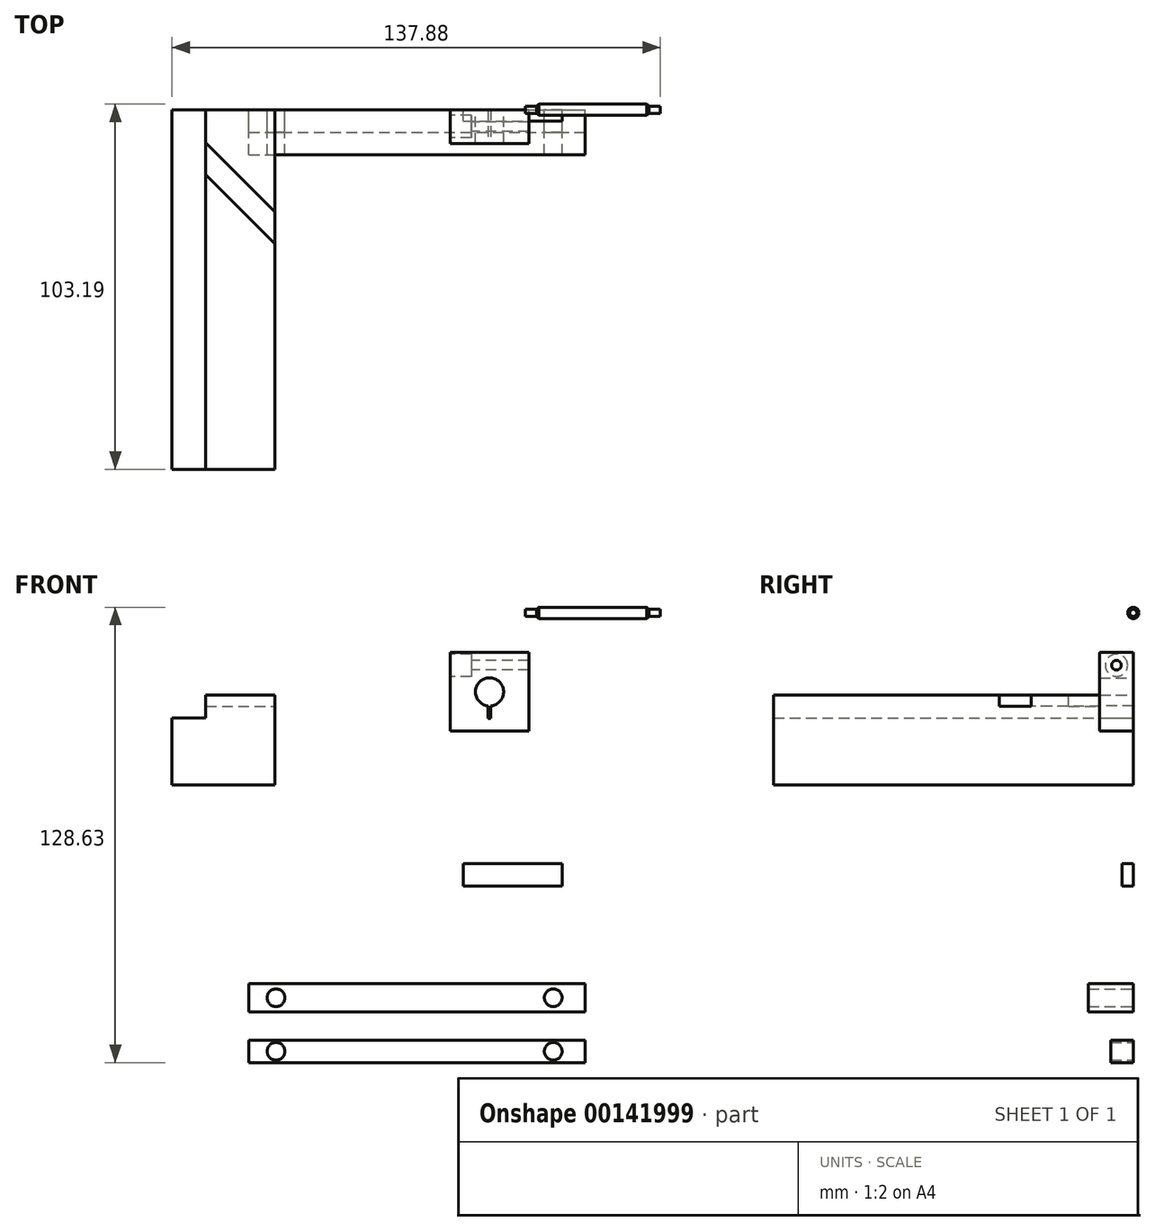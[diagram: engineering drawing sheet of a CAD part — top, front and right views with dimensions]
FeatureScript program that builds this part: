
annotation { "Feature Type Name" : "Feature", "Feature Type Description" : "" }
export const myFeature = defineFeature(function(context is Context, id is Id, definition is map)
    precondition{}
    {
        {
            var Q0;
            Q0=qCreatedBy(makeId("Front.planeOp"),FACE);
            var sketch = newSketch(context, id + "F0", { "sketchPlane" : qUnion([Q0])});
            skCircle(sketch, "E0", {"center": v(-55.23, 48.48) * mm, "radius": 3.97 * mm});
            skLineSegment(sketch, "E1.bottom", {"start": v(-44.12, 37.37) * mm, "end": v(-66.34, 37.37) * mm});
            skLineSegment(sketch, "E1.top", {"start": v(-44.12, 59.6) * mm, "end": v(-66.34, 59.6) * mm});
            skLineSegment(sketch, "E1.left", {"start": v(-44.12, 37.37) * mm, "end": v(-44.12, 59.6) * mm});
            skLineSegment(sketch, "E1.right", {"start": v(-66.34, 37.37) * mm, "end": v(-66.34, 59.6) * mm});
            skSolve(sketch);
        }
        {
            var Q0;
            Q0=makeQuery(id+"F0.imprint","IMPRINT",FACE,{"disambiguationData":[TD([[makeQuery(id+"F0.imprint","IMPRINT",EDGE,{"derivedFrom":sQuery(id+"F0.wireOp",EDGE,"E0")}),-1.0]])]});
            extrude(context, id + "F1", {"entities" : qUnion([Q0]), "depth" : 9.52 * mm});
        }
        {
            var Q0;
            Q0=makeQuery(id+"F1.opExtrude","SWEPT_FACE",FACE,{"disambiguationData":[OSD([sQuery(id+"F0.wireOp",EDGE,"E1.right")])]});
            var sketch = newSketch(context, id + "F2", { "sketchPlane" : qUnion([Q0])});
            skLineSegment(sketch, "E2.0", {"start": v(9.53, 59.6) * mm, "end": v(0, 59.6) * mm});
            skLineSegment(sketch, "E3.0", {"start": v(9.53, 37.37) * mm, "end": v(0, 37.37) * mm});
            skLineSegment(sketch, "E4", {"start": v(4.76, 59.6) * mm, "end": v(4.76, 52.45) * mm, "construction": true});
            skCircle(sketch, "E5", {"center": v(4.76, 48.48) * mm, "radius": 3.97 * mm});
            skLineSegment(sketch, "E6.trimOffspring", {"start": v(4.76, 44.51) * mm, "end": v(4.76, 37.37) * mm, "construction": true});
            skLineSegment(sketch, "E7", {"start": v(4.76, 48.48) * mm, "end": v(9.53, 48.48) * mm, "construction": true});
            skPoint(sketch, "E8", {"position": v(4.76, 56.02) * mm});
            skSolve(sketch);
        }
        {
            var Q0;
            Q0=sQuery(id+"F2.wireOp",VERTEX,"E8");
            var Q1;
            Q1=makeQuery(id+"F1.opExtrude","SWEPT_BODY",BODY,{"disambiguationData":[OSD([sQuery(id+"F0.wireOp",EDGE,"E0"),sQuery(id+"F0.wireOp",EDGE,"E1.bottom"),sQuery(id+"F0.wireOp",EDGE,"E1.top"),sQuery(id+"F0.wireOp",EDGE,"E1.left"),sQuery(id+"F0.wireOp",EDGE,"E1.right")])]});
            hole(context, id + "F3", {"style" : HoleStyle.C_BORE, "endStyle" : HoleEndStyle.THROUGH, "holeDiameter" : 2.7 * mm, "cBoreDiameter" : 6.35 * mm, "cBoreDepth" : 5.97 * mm, "tappedDepth" : 12.7 * mm, "tapClearance" : 3, "startFromSketch" : true, "locations" : qUnion([Q0]), "scope" : qUnion([Q1]), "majorDiameter" : 6.35 * mm});
        }
        {
            var Q0;
            Q0=makeQuery(id+"F1.opExtrude","CAP_FACE",FACE,{"disambiguationData":[OSD([sQuery(id+"F0.wireOp",EDGE,"E0"),sQuery(id+"F0.wireOp",EDGE,"E1.bottom"),sQuery(id+"F0.wireOp",EDGE,"E1.top"),sQuery(id+"F0.wireOp",EDGE,"E1.left"),sQuery(id+"F0.wireOp",EDGE,"E1.right")])],"isStart":false});
            var sketch = newSketch(context, id + "F4", { "sketchPlane" : qUnion([Q0])});
            skLineSegment(sketch, "E9.0", {"start": v(-44.12, 59.6) * mm, "end": v(-66.34, 59.6) * mm});
            skLineSegment(sketch, "E10.0", {"start": v(-44.12, 37.37) * mm, "end": v(-44.12, 59.6) * mm});
            skLineSegment(sketch, "E11.0", {"start": v(-66.34, 37.37) * mm, "end": v(-66.34, 59.6) * mm});
            skLineSegment(sketch, "E12.0", {"start": v(-44.12, 37.37) * mm, "end": v(-66.34, 37.37) * mm});
            skLineSegment(sketch, "E13", {"start": v(-55.63, 59.6) * mm, "end": v(-54.83, 59.6) * mm});
            skLineSegment(sketch, "E14", {"start": v(-55.23, 59.6) * mm, "end": v(-55.23, 48.48) * mm, "construction": true});
            skLineSegment(sketch, "E15.0", {"start": v(-55.63, 59.6) * mm, "end": v(-55.63, 40.94) * mm});
            skLineSegment(sketch, "E16.0", {"start": v(-54.83, 59.6) * mm, "end": v(-54.83, 40.94) * mm});
            skCircle(sketch, "E17.0", {"center": v(-55.23, 48.48) * mm, "radius": 3.97 * mm});
            skLineSegment(sketch, "E18.trimOffspring", {"start": v(-55.23, 44.51) * mm, "end": v(-55.23, 37.37) * mm, "construction": true});
            skLineSegment(sketch, "E19", {"start": v(-55.63, 40.94) * mm, "end": v(-54.83, 40.94) * mm});
            skPoint(sketch, "E19.startSnap0", {"position": v(-55.23, 40.94) * mm});
            skSolve(sketch);
        }
        {
            var Q0;
            {var subQ5=sQuery(id+"F4.wireOp",EDGE,"E13");Q0=makeQuery(id+"F4.imprint","IMPRINT",FACE,{"disambiguationData":[TD([[makeQuery(id+"F4.imprint","IMPRINT",EDGE,{"derivedFrom":subQ5}),1.0]])]});}
            var Q1;
            {var subQ0=sQuery(id+"F4.wireOp",EDGE,"E19");Q1=makeQuery(id+"F4.imprint","IMPRINT",FACE,{"disambiguationData":[TD([[makeQuery(id+"F4.imprint","IMPRINT",EDGE,{"derivedFrom":subQ0}),1.0]])]});}
            extrude(context, id + "F5", {"entities" : qUnion([Q0, Q1]), "operationType" : NewBodyOperationType.REMOVE, "oppositeDirection" : true, "depth" : 25.4 * mm});
        }
        {
            var Q0;
            Q0=qCreatedBy(makeId("Front.planeOp"),FACE);
            var sketch = newSketch(context, id + "F6", { "sketchPlane" : qUnion([Q0])});
            skLineSegment(sketch, "E20", {"start": v(-45.1, 70.79) * mm, "end": v(-7, 70.79) * mm});
            skLineSegment(sketch, "E21", {"start": v(-45.1, 70.79) * mm, "end": v(-45.1, 71.78) * mm});
            skLineSegment(sketch, "E22", {"start": v(-41.34, 72.38) * mm, "end": v(-10.78, 72.38) * mm});
            skLineSegment(sketch, "E23", {"start": v(-10.78, 72.38) * mm, "end": v(-10.18, 71.78) * mm});
            skLineSegment(sketch, "E24", {"start": v(-10.18, 71.78) * mm, "end": v(-7, 71.78) * mm});
            skLineSegment(sketch, "E25", {"start": v(-7, 71.78) * mm, "end": v(-7, 70.79) * mm});
            skLineSegment(sketch, "E26", {"start": v(-26.06, 70.79) * mm, "end": v(-26.06, 72.38) * mm, "construction": true});
            skLineSegment(sketch, "E27.MirrorCS", {"start": v(-41.34, 72.38) * mm, "end": v(-41.93, 71.78) * mm});
            skLineSegment(sketch, "E28.MirrorCS", {"start": v(-41.93, 71.78) * mm, "end": v(-45.1, 71.78) * mm});
            skLineSegment(sketch, "E29.MirrorCS", {"start": v(-45.1, 71.78) * mm, "end": v(-45.1, 70.79) * mm});
            skSolve(sketch);
        }
        {
            var Q0;
            Q0=makeQuery(id+"F6.imprint","IMPRINT",FACE,{"disambiguationData":[TD([[makeQuery(id+"F6.imprint","IMPRINT",EDGE,{"derivedFrom":sQuery(id+"F6.wireOp",EDGE,"E20")}),1.0]])]});
            var Q1;
            Q1=sQuery(id+"F6.wireOp",EDGE,"E22");
            var Q2;
            Q2=sQuery(id+"F6.wireOp",EDGE,"E27.MirrorCS");
            var Q3;
            Q3=sQuery(id+"F6.wireOp",EDGE,"E28.MirrorCS");
            var Q4;
            Q4=sQuery(id+"F6.wireOp",EDGE,"E29.MirrorCS");
            var Q5;
            Q5=sQuery(id+"F6.wireOp",EDGE,"E23");
            var Q6;
            Q6=sQuery(id+"F6.wireOp",EDGE,"E24");
            var Q7;
            Q7=sQuery(id+"F6.wireOp",EDGE,"E25");
            var Q8;
            Q8=sQuery(id+"F6.wireOp",EDGE,"E20");
            revolve(context, id + "F7", {"entities" : qUnion([Q0]), "surfaceEntities" : qUnion([Q1, Q2, Q3, Q4, Q5, Q6, Q7]), "axis" : qUnion([Q8]), "revolveType" : RevolveType.FULL});
        }
        {
            var Q0;
            Q0=qCreatedBy(makeId("Front.planeOp"),FACE);
            var sketch = newSketch(context, id + "F8", { "sketchPlane" : qUnion([Q0])});
            skLineSegment(sketch, "E30.bottom", {"start": v(-123.23, -33.97) * mm, "end": v(-28.24, -33.97) * mm});
            skLineSegment(sketch, "E30.top", {"start": v(-123.23, -41.9) * mm, "end": v(-28.24, -41.9) * mm});
            skLineSegment(sketch, "E30.left", {"start": v(-123.23, -33.97) * mm, "end": v(-123.23, -41.9) * mm});
            skLineSegment(sketch, "E30.right", {"start": v(-28.24, -33.97) * mm, "end": v(-28.24, -41.9) * mm});
            skLineSegment(sketch, "E31", {"start": v(-123.23, -37.93) * mm, "end": v(-28.24, -37.93) * mm, "construction": true});
            skCircle(sketch, "E32", {"center": v(-115.54, -37.93) * mm, "radius": 2.5 * mm});
            skCircle(sketch, "E33", {"center": v(-37.23, -37.93) * mm, "radius": 2.5 * mm});
            skSolve(sketch);
        }
        {
            var Q0;
            Q0 = qSketchRegion(id + "F8", true);
            extrude(context, id + "F9", {"entities" : qUnion([Q0]), "depth" : 12.7 * mm});
        }
        {
            var Q0;
            Q0=qCreatedBy(makeId("Front.planeOp"),FACE);
            var sketch = newSketch(context, id + "F10", { "sketchPlane" : qUnion([Q0])});
            skLineSegment(sketch, "E34.0", {"start": v(-123.23, -33.97) * mm, "end": v(-123.23, -41.9) * mm});
            skLineSegment(sketch, "E35.0", {"start": v(-123.23, -41.9) * mm, "end": v(-28.24, -41.9) * mm});
            skLineSegment(sketch, "E36.0", {"start": v(-28.24, -33.97) * mm, "end": v(-28.24, -41.9) * mm});
            skCircle(sketch, "E37.0", {"center": v(-37.23, -37.93) * mm, "radius": 2.5 * mm});
            skCircle(sketch, "E38.0", {"center": v(-115.54, -37.93) * mm, "radius": 2.5 * mm});
            skLineSegment(sketch, "E39.bottom", {"start": v(-123.23, -49.9) * mm, "end": v(-28.24, -49.9) * mm});
            skLineSegment(sketch, "E39.top", {"start": v(-123.23, -56.25) * mm, "end": v(-28.24, -56.25) * mm});
            skLineSegment(sketch, "E39.left", {"start": v(-123.23, -49.9) * mm, "end": v(-123.23, -56.25) * mm});
            skLineSegment(sketch, "E39.right", {"start": v(-28.24, -49.9) * mm, "end": v(-28.24, -56.25) * mm});
            skLineSegment(sketch, "E40", {"start": v(-123.23, -53.08) * mm, "end": v(-28.24, -53.08) * mm, "construction": true});
            skCircle(sketch, "E41", {"center": v(-115.54, -53.08) * mm, "radius": 2.5 * mm});
            skCircle(sketch, "E42", {"center": v(-37.23, -53.08) * mm, "radius": 2.5 * mm});
            skSolve(sketch);
        }
        {
            var Q0;
            Q0=makeQuery(id+"F10.imprint","IMPRINT",FACE,{"disambiguationData":[TD([[makeQuery(id+"F10.imprint","IMPRINT",EDGE,{"derivedFrom":sQuery(id+"F10.wireOp",EDGE,"E39.bottom")}),-1.0]])]});
            extrude(context, id + "F11", {"entities" : qUnion([Q0]), "depth" : 6.35 * mm});
        }
        {
            var Q0;
            Q0=qCreatedBy(makeId("Front.planeOp"),FACE);
            var sketch = newSketch(context, id + "F12", { "sketchPlane" : qUnion([Q0])});
            skLineSegment(sketch, "E43.bottom", {"start": v(-62.62, 0) * mm, "end": v(-34.69, 0) * mm});
            skLineSegment(sketch, "E43.top", {"start": v(-62.62, -6.35) * mm, "end": v(-34.69, -6.35) * mm});
            skLineSegment(sketch, "E43.left", {"start": v(-62.62, 0) * mm, "end": v(-62.62, -6.35) * mm});
            skLineSegment(sketch, "E43.right", {"start": v(-34.69, 0) * mm, "end": v(-34.69, -6.35) * mm});
            skSolve(sketch);
        }
        {
            var Q0;
            Q0 = qSketchRegion(id + "F12", true);
            extrude(context, id + "F13", {"entities" : qUnion([Q0]), "depth" : 3.17 * mm});
        }
        {
            var Q0;
            Q0=qCreatedBy(makeId("Front.planeOp"),FACE);
            var sketch = newSketch(context, id + "F14", { "sketchPlane" : qUnion([Q0])});
            skLineSegment(sketch, "E44.bottom", {"start": v(-135.36, 47.6) * mm, "end": v(-115.83, 47.6) * mm});
            skLineSegment(sketch, "E44.top", {"start": v(-144.89, 22.2) * mm, "end": v(-115.83, 22.2) * mm});
            skLineSegment(sketch, "E44.left", {"start": v(-144.89, 41.1) * mm, "end": v(-144.89, 22.2) * mm});
            skLineSegment(sketch, "E44.right", {"start": v(-115.83, 47.6) * mm, "end": v(-115.83, 22.2) * mm});
            skLineSegment(sketch, "E45", {"start": v(-135.36, 47.6) * mm, "end": v(-135.36, 41.1) * mm});
            skLineSegment(sketch, "E46", {"start": v(-135.36, 41.1) * mm, "end": v(-144.89, 41.1) * mm});
            skSolve(sketch);
        }
        {
            var Q0;
            Q0=makeQuery(id+"F14.imprint","IMPRINT",FACE,{"disambiguationData":[TD([[makeQuery(id+"F14.imprint","IMPRINT",EDGE,{"derivedFrom":sQuery(id+"F14.wireOp",EDGE,"E44.bottom")}),-1.0]])]});
            extrude(context, id + "F15", {"entities" : qUnion([Q0]), "depth" : 101.6 * mm, "offsetDistance" : 25.4 * mm});
        }
        {
            var Q0;
            Q0=makeQuery(id+"F15.opExtrude","SWEPT_FACE",FACE,{"disambiguationData":[OSD([sQuery(id+"F14.wireOp",EDGE,"E44.bottom")])]});
            var sketch = newSketch(context, id + "F16", { "sketchPlane" : qUnion([Q0])});
            skLineSegment(sketch, "E47", {"start": v(-135.36, -18.3) * mm, "end": v(-115.83, -37.83) * mm});
            skLineSegment(sketch, "E48", {"start": v(-135.36, -9.32) * mm, "end": v(-115.83, -28.85) * mm});
            skLineSegment(sketch, "E49", {"start": v(-135.36, -9.32) * mm, "end": v(-135.36, -18.3) * mm});
            skLineSegment(sketch, "E50", {"start": v(-115.83, -28.85) * mm, "end": v(-115.83, -37.83) * mm});
            skSolve(sketch);
        }
        {
            var Q0;
            Q0 = qSketchRegion(id + "F16", true);
            var Q1;
            Q1=makeQuery(id+"F16.imprint","IMPRINT",FACE,{"disambiguationData":[TD([[makeQuery(id+"F16.imprint","IMPRINT",EDGE,{"derivedFrom":sQuery(id+"F16.wireOp",EDGE,"E47")}),1.0]])]});
            extrude(context, id + "F17", {"entities" : qUnion([Q0, Q1]), "operationType" : NewBodyOperationType.REMOVE, "oppositeDirection" : true, "depth" : 3.17 * mm, "offsetDistance" : 25.4 * mm});
        }
    });
